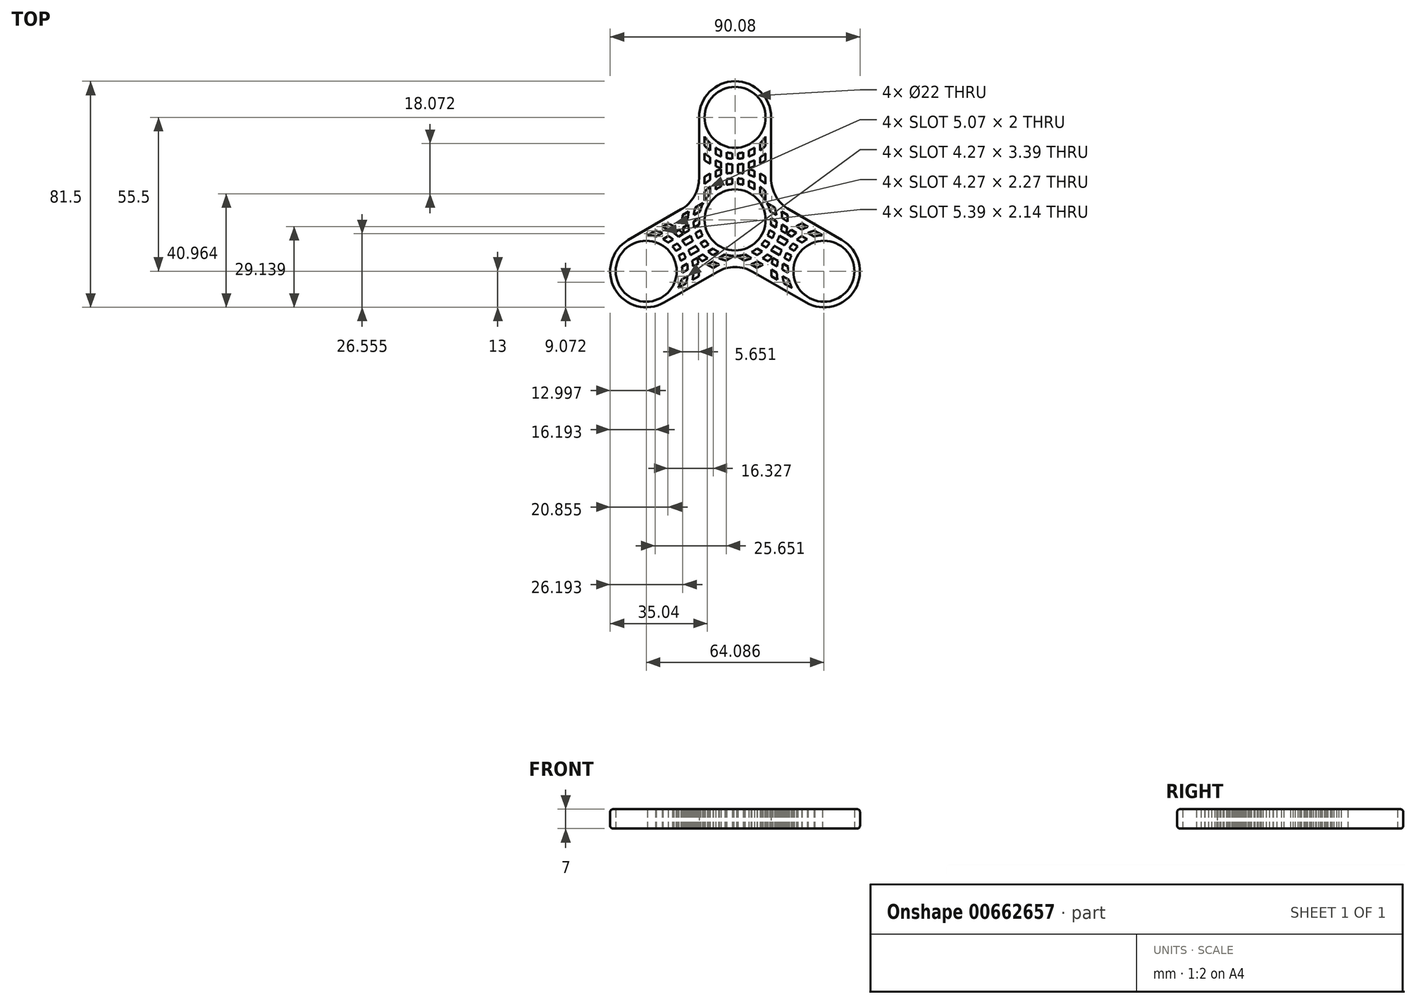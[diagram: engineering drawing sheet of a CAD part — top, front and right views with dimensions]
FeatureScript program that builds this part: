
annotation { "Feature Type Name" : "Feature", "Feature Type Description" : "" }
export const myFeature = defineFeature(function(context is Context, id is Id, definition is map)
    precondition{}
    {
        {
            var Q0;
            Q0=qCreatedBy(makeId("Top.planeOp"),FACE);
            var sketch = newSketch(context, id + "F0", { "sketchPlane" : qUnion([Q0])});
            skCircle(sketch, "E0", {"center": v(0, 0) * mm, "radius": 11 * mm});
            skCircle(sketch, "E1", {"center": v(0, 37) * mm, "radius": 11 * mm});
            skLineSegment(sketch, "E2", {"start": v(13, 37) * mm, "end": v(13, 15.01) * mm});
            skLineSegment(sketch, "E3.MirrorCS", {"start": v(-13, 37) * mm, "end": v(-13, 15.01) * mm});
            skLineSegment(sketch, "E4.1.0.0", {"start": v(-11, 30.07) * mm, "end": v(-11, 26.8) * mm});
            skLineSegment(sketch, "E4.2.0.0", {"start": v(-9, 27.62) * mm, "end": v(-9, 25) * mm});
            skLineSegment(sketch, "E4.3.0.0", {"start": v(-7, 26.05) * mm, "end": v(-7, 23.73) * mm});
            skLineSegment(sketch, "E4.4.0.0", {"start": v(-5, 25) * mm, "end": v(-5, 22.86) * mm});
            skLineSegment(sketch, "E4.5.0.0", {"start": v(-3, 24.35) * mm, "end": v(-3, 22.3) * mm});
            skLineSegment(sketch, "E4.6.0.0", {"start": v(-1, 24.04) * mm, "end": v(-1, 22.03) * mm});
            skLineSegment(sketch, "E4.7.0.0", {"start": v(1, 24.04) * mm, "end": v(1, 22.03) * mm});
            skLineSegment(sketch, "E4.8.0.0", {"start": v(3, 24.35) * mm, "end": v(3, 22.3) * mm});
            skLineSegment(sketch, "E4.9.0.0", {"start": v(5, 25) * mm, "end": v(5, 22.86) * mm});
            skLineSegment(sketch, "E4.10.0.0", {"start": v(7, 26.05) * mm, "end": v(7, 23.73) * mm});
            skLineSegment(sketch, "E4.11.0.0", {"start": v(9, 27.62) * mm, "end": v(9, 25) * mm});
            skLineSegment(sketch, "E4.12.0.0", {"start": v(11, 30.07) * mm, "end": v(11, 26.8) * mm});
            skArc(sketch, "E5", {"start": v(-11, 30.07) * mm, "mid": v(-10.07, 28.78) * mm, "end": v(-9, 27.62) * mm});
            skArc(sketch, "E6", {"start": v(-9, 9.38) * mm, "mid": v(-10.07, 8.22) * mm, "end": v(-11, 6.93) * mm});
            skArc(sketch, "E7.trimOffspring", {"start": v(13, 37) * mm, "mid": v(0, 50) * mm, "end": v(-13, 37) * mm});
            skArc(sketch, "E8.trimOffspring", {"start": v(9, 27.62) * mm, "mid": v(10.07, 28.78) * mm, "end": v(11, 30.07) * mm});
            skArc(sketch, "E9.trimOffspring", {"start": v(-7, 26.05) * mm, "mid": v(-6.02, 25.48) * mm, "end": v(-5, 25) * mm});
            skArc(sketch, "E10.trimOffspring", {"start": v(-3, 24.35) * mm, "mid": v(-2, 24.16) * mm, "end": v(-1, 24.04) * mm});
            skArc(sketch, "E11.trimOffspring", {"start": v(1, 24.04) * mm, "mid": v(2, 24.16) * mm, "end": v(3, 24.35) * mm});
            skArc(sketch, "E12.trimOffspring", {"start": v(5, 25) * mm, "mid": v(6.02, 25.48) * mm, "end": v(7, 26.05) * mm});
            skArc(sketch, "E13.trimOffspring", {"start": v(-5, 12) * mm, "mid": v(-6.02, 11.52) * mm, "end": v(-7, 10.95) * mm});
            skArc(sketch, "E14.trimOffspring", {"start": v(-1, 12.96) * mm, "mid": v(-2, 12.84) * mm, "end": v(-3, 12.65) * mm});
            skArc(sketch, "E15.trimOffspring", {"start": v(3, 12.65) * mm, "mid": v(2, 12.84) * mm, "end": v(1, 12.96) * mm});
            skArc(sketch, "E16.trimOffspring", {"start": v(7, 10.95) * mm, "mid": v(6.02, 11.52) * mm, "end": v(5, 12) * mm});
            skArc(sketch, "E17", {"start": v(11, 10.2) * mm, "mid": v(10.04, 11.14) * mm, "end": v(9, 12) * mm});
            skArc(sketch, "E18", {"start": v(-11, 26.8) * mm, "mid": v(-10.04, 25.86) * mm, "end": v(-9, 25) * mm});
            skArc(sketch, "E19", {"start": v(-11, 24.04) * mm, "mid": v(-10.03, 23.27) * mm, "end": v(-9, 22.58) * mm});
            skArc(sketch, "E20.trimOffspring", {"start": v(-7, 23.73) * mm, "mid": v(-6.02, 23.26) * mm, "end": v(-5, 22.86) * mm});
            skArc(sketch, "E21.trimOffspring", {"start": v(-7, 21.5) * mm, "mid": v(-6.01, 21.1) * mm, "end": v(-5, 20.75) * mm});
            skArc(sketch, "E22.trimOffspring", {"start": v(-3, 22.3) * mm, "mid": v(-2, 22.13) * mm, "end": v(-1, 22.03) * mm});
            skArc(sketch, "E23.trimOffspring", {"start": v(-3, 20.27) * mm, "mid": v(-2, 20.12) * mm, "end": v(-1, 20.03) * mm});
            skArc(sketch, "E24.trimOffspring", {"start": v(1, 20.03) * mm, "mid": v(2, 20.12) * mm, "end": v(3, 20.27) * mm});
            skArc(sketch, "E25.trimOffspring", {"start": v(1, 22.03) * mm, "mid": v(2, 22.13) * mm, "end": v(3, 22.3) * mm});
            skArc(sketch, "E26.trimOffspring", {"start": v(5, 22.86) * mm, "mid": v(6.02, 23.26) * mm, "end": v(7, 23.73) * mm});
            skArc(sketch, "E27.trimOffspring", {"start": v(5, 20.75) * mm, "mid": v(6.01, 21.1) * mm, "end": v(7, 21.5) * mm});
            skArc(sketch, "E28.trimOffspring", {"start": v(9, 25) * mm, "mid": v(10.04, 25.86) * mm, "end": v(11, 26.8) * mm});
            skArc(sketch, "E29.trimOffspring", {"start": v(9, 22.58) * mm, "mid": v(10.03, 23.27) * mm, "end": v(11, 24.04) * mm});
            skArc(sketch, "E30.trimOffspring", {"start": v(11, 12.96) * mm, "mid": v(10.03, 13.73) * mm, "end": v(9, 14.42) * mm});
            skArc(sketch, "E31.trimOffspring", {"start": v(-9, 14.42) * mm, "mid": v(-10.03, 13.73) * mm, "end": v(-11, 12.96) * mm});
            skArc(sketch, "E32.trimOffspring", {"start": v(-9, 12) * mm, "mid": v(-10.04, 11.14) * mm, "end": v(-11, 10.2) * mm});
            skArc(sketch, "E33.trimOffspring", {"start": v(-5, 14.14) * mm, "mid": v(-6.02, 13.74) * mm, "end": v(-7, 13.27) * mm});
            skArc(sketch, "E34.trimOffspring", {"start": v(-5, 16.25) * mm, "mid": v(-6.01, 15.9) * mm, "end": v(-7, 15.5) * mm});
            skArc(sketch, "E35.trimOffspring", {"start": v(-1, 16.97) * mm, "mid": v(-2, 16.88) * mm, "end": v(-3, 16.73) * mm});
            skArc(sketch, "E36.trimOffspring", {"start": v(-1, 14.97) * mm, "mid": v(-2, 14.87) * mm, "end": v(-3, 14.7) * mm});
            skArc(sketch, "E37.trimOffspring", {"start": v(3, 16.73) * mm, "mid": v(2, 16.88) * mm, "end": v(1, 16.97) * mm});
            skArc(sketch, "E38.trimOffspring", {"start": v(3, 14.7) * mm, "mid": v(2, 14.87) * mm, "end": v(1, 14.97) * mm});
            skArc(sketch, "E39.trimOffspring", {"start": v(7, 15.5) * mm, "mid": v(6.01, 15.9) * mm, "end": v(5, 16.25) * mm});
            skArc(sketch, "E40.trimOffspring", {"start": v(7, 13.27) * mm, "mid": v(6.02, 13.74) * mm, "end": v(5, 14.14) * mm});
            skLineSegment(sketch, "E41.trimOffspring", {"start": v(-11, 24.04) * mm, "end": v(-11, 21.5) * mm});
            skLineSegment(sketch, "E42.trimOffspring", {"start": v(-9, 22.58) * mm, "end": v(-9, 20.27) * mm});
            skLineSegment(sketch, "E43.trimOffspring", {"start": v(-7, 21.5) * mm, "end": v(-7, 19.34) * mm});
            skLineSegment(sketch, "E44.trimOffspring", {"start": v(-5, 20.75) * mm, "end": v(-5, 18.67) * mm});
            skLineSegment(sketch, "E45.trimOffspring", {"start": v(-3, 20.27) * mm, "end": v(-3, 16.73) * mm});
            skLineSegment(sketch, "E46.trimOffspring", {"start": v(-1, 20.03) * mm, "end": v(-1, 16.97) * mm});
            skLineSegment(sketch, "E47.trimOffspring", {"start": v(1, 20.03) * mm, "end": v(1, 16.97) * mm});
            skLineSegment(sketch, "E48.trimOffspring", {"start": v(3, 20.27) * mm, "end": v(3, 16.73) * mm});
            skLineSegment(sketch, "E49.trimOffspring", {"start": v(5, 20.75) * mm, "end": v(5, 18.67) * mm});
            skLineSegment(sketch, "E50.trimOffspring", {"start": v(7, 21.5) * mm, "end": v(7, 19.34) * mm});
            skLineSegment(sketch, "E51.trimOffspring", {"start": v(9, 22.58) * mm, "end": v(9, 20.27) * mm});
            skLineSegment(sketch, "E52.trimOffspring", {"start": v(11, 24.04) * mm, "end": v(11, 21.5) * mm});
            skLineSegment(sketch, "E53.trimOffspring", {"start": v(-11, 10.2) * mm, "end": v(-11, 6.93) * mm});
            skLineSegment(sketch, "E54.trimOffspring", {"start": v(-7, 13.27) * mm, "end": v(-7, 10.95) * mm});
            skLineSegment(sketch, "E55.trimOffspring", {"start": v(-3, 14.7) * mm, "end": v(-3, 12.65) * mm});
            skLineSegment(sketch, "E56.trimOffspring", {"start": v(1, 14.97) * mm, "end": v(1, 12.96) * mm});
            skLineSegment(sketch, "E57.trimOffspring", {"start": v(5, 14.14) * mm, "end": v(5, 12) * mm});
            skLineSegment(sketch, "E58.trimOffspring", {"start": v(9, 12) * mm, "end": v(9, 9.38) * mm});
            skLineSegment(sketch, "E59.trimOffspring", {"start": v(-9, 12) * mm, "end": v(-9, 9.38) * mm});
            skLineSegment(sketch, "E60.trimOffspring", {"start": v(-5, 14.14) * mm, "end": v(-5, 12) * mm});
            skLineSegment(sketch, "E61.trimOffspring", {"start": v(-1, 14.97) * mm, "end": v(-1, 12.96) * mm});
            skLineSegment(sketch, "E62.trimOffspring", {"start": v(3, 14.7) * mm, "end": v(3, 12.65) * mm});
            skLineSegment(sketch, "E63.trimOffspring", {"start": v(7, 13.27) * mm, "end": v(7, 10.95) * mm});
            skLineSegment(sketch, "E64.trimOffspring", {"start": v(11, 10.2) * mm, "end": v(11, 6.93) * mm});
            skArc(sketch, "E65", {"start": v(-11, 21.5) * mm, "mid": v(-10.02, 20.86) * mm, "end": v(-9, 20.27) * mm});
            skArc(sketch, "E66.trimOffspring", {"start": v(11, 15.5) * mm, "mid": v(10.02, 16.14) * mm, "end": v(9, 16.73) * mm});
            skArc(sketch, "E67.trimOffspring", {"start": v(-7, 19.34) * mm, "mid": v(-6, 18.98) * mm, "end": v(-5, 18.67) * mm});
            skArc(sketch, "E68.trimOffspring", {"start": v(-9, 16.73) * mm, "mid": v(-10.02, 16.14) * mm, "end": v(-11, 15.5) * mm});
            skArc(sketch, "E69.trimOffspring", {"start": v(9, 20.27) * mm, "mid": v(10.02, 20.86) * mm, "end": v(11, 21.5) * mm});
            skArc(sketch, "E70.trimOffspring", {"start": v(7, 17.66) * mm, "mid": v(6, 18.02) * mm, "end": v(5, 18.33) * mm});
            skArc(sketch, "E71.trimOffspring", {"start": v(-5, 18.33) * mm, "mid": v(-6, 18.02) * mm, "end": v(-7, 17.66) * mm});
            skArc(sketch, "E72.trimOffspring", {"start": v(5, 18.67) * mm, "mid": v(6, 18.98) * mm, "end": v(7, 19.34) * mm});
            skLineSegment(sketch, "E73.trimOffspring", {"start": v(-11, 15.5) * mm, "end": v(-11, 12.96) * mm});
            skLineSegment(sketch, "E74.trimOffspring", {"start": v(-9, 16.73) * mm, "end": v(-9, 14.42) * mm});
            skLineSegment(sketch, "E75.trimOffspring", {"start": v(11, 15.5) * mm, "end": v(11, 12.96) * mm});
            skLineSegment(sketch, "E76.trimOffspring", {"start": v(9, 16.73) * mm, "end": v(9, 14.42) * mm});
            skLineSegment(sketch, "E77.trimOffspring", {"start": v(-7, 17.66) * mm, "end": v(-7, 15.5) * mm});
            skLineSegment(sketch, "E78.trimOffspring", {"start": v(-5, 18.33) * mm, "end": v(-5, 16.25) * mm});
            skLineSegment(sketch, "E79.trimOffspring", {"start": v(5, 18.33) * mm, "end": v(5, 16.25) * mm});
            skLineSegment(sketch, "E80.trimOffspring", {"start": v(7, 17.66) * mm, "end": v(7, 15.5) * mm});
            skArc(sketch, "E81.trimOffspring", {"start": v(11, 6.93) * mm, "mid": v(10.07, 8.22) * mm, "end": v(9, 9.38) * mm});
            skCircle(sketch, "E82.1.0", {"center": v(-32.04, -18.5) * mm, "radius": 11 * mm});
            skLineSegment(sketch, "E82.1.1", {"start": v(-31.54, -5.5) * mm, "end": v(-28.71, -3.87) * mm});
            skLineSegment(sketch, "E82.1.2", {"start": v(-38.54, -7.24) * mm, "end": v(-19.5, 3.75) * mm});
            skLineSegment(sketch, "E82.1.3", {"start": v(-25.54, -29.76) * mm, "end": v(-6.5, -18.76) * mm});
            skLineSegment(sketch, "E82.1.4", {"start": v(-20.54, -24.56) * mm, "end": v(-17.71, -22.93) * mm});
            skArc(sketch, "E82.1.5", {"start": v(-38.54, -7.24) * mm, "mid": v(-43.3, -25) * mm, "end": v(-25.54, -29.76) * mm});
            skLineSegment(sketch, "E82.1.6", {"start": v(-14.33, 4.43) * mm, "end": v(-11.5, 6.06) * mm});
            skLineSegment(sketch, "E82.1.7", {"start": v(-19.05, -7.54) * mm, "end": v(-16, -5.77) * mm});
            skArc(sketch, "E82.1.8", {"start": v(-20.54, -24.56) * mm, "mid": v(-19.9, -23.12) * mm, "end": v(-19.42, -21.6) * mm});
            skLineSegment(sketch, "E82.1.9", {"start": v(-3.33, -14.63) * mm, "end": v(-0.5, -13) * mm});
            skLineSegment(sketch, "E82.1.10", {"start": v(-16.05, -12.73) * mm, "end": v(-13, -10.96) * mm});
            skArc(sketch, "E82.1.11", {"start": v(-28.42, -6.02) * mm, "mid": v(-29.97, -5.67) * mm, "end": v(-31.54, -5.5) * mm});
            skLineSegment(sketch, "E82.1.12", {"start": v(-17.85, -9.15) * mm, "end": v(-15.2, -7.62) * mm});
            skLineSegment(sketch, "E82.1.13", {"start": v(-16.85, -10.88) * mm, "end": v(-14.2, -9.35) * mm});
            skLineSegment(sketch, "E82.1.14", {"start": v(-10, -16.16) * mm, "end": v(-7.99, -15) * mm});
            skLineSegment(sketch, "E82.1.15", {"start": v(-11.23, -9.95) * mm, "end": v(-9.45, -8.92) * mm});
            skArc(sketch, "E82.1.16", {"start": v(-14.33, 4.43) * mm, "mid": v(-14.67, 3.12) * mm, "end": v(-14.9, 1.8) * mm});
            skLineSegment(sketch, "E82.1.17", {"start": v(-22.13, -4.7) * mm, "end": v(-20.25, -3.6) * mm});
            skArc(sketch, "E82.1.18", {"start": v(-20.47, -6.05) * mm, "mid": v(-21.28, -5.34) * mm, "end": v(-22.13, -4.7) * mm});
            skArc(sketch, "E82.1.19", {"start": v(-24.15, -8.17) * mm, "mid": v(-25.08, -7.52) * mm, "end": v(-26.06, -6.96) * mm});
            skLineSegment(sketch, "E82.1.20", {"start": v(-15.13, -16.82) * mm, "end": v(-13.25, -15.73) * mm});
            skLineSegment(sketch, "E82.1.21", {"start": v(-26.32, -2.5) * mm, "end": v(-24.13, -1.23) * mm});
            skArc(sketch, "E82.1.22", {"start": v(-12.46, -8.35) * mm, "mid": v(-11.87, -9.17) * mm, "end": v(-11.23, -9.95) * mm});
            skLineSegment(sketch, "E82.1.23", {"start": v(-22.59, -9.58) * mm, "end": v(-20.82, -8.55) * mm});
            skLineSegment(sketch, "E82.1.24", {"start": v(-26.06, -6.96) * mm, "end": v(-24.05, -5.8) * mm});
            skArc(sketch, "E82.1.25", {"start": v(-10, -16.16) * mm, "mid": v(-8.97, -16.75) * mm, "end": v(-7.92, -17.27) * mm});
            skLineSegment(sketch, "E82.1.26", {"start": v(-18.92, 1.78) * mm, "end": v(-16.72, 3.05) * mm});
            skArc(sketch, "E82.1.27", {"start": v(-19.59, -14.77) * mm, "mid": v(-19.92, -13.82) * mm, "end": v(-20.32, -12.89) * mm});
            skLineSegment(sketch, "E82.1.28", {"start": v(-5.9, -13.8) * mm, "end": v(-3.62, -12.48) * mm});
            skArc(sketch, "E82.1.29", {"start": v(-21.32, -11.15) * mm, "mid": v(-21.92, -10.34) * mm, "end": v(-22.59, -9.58) * mm});
            skLineSegment(sketch, "E82.1.30", {"start": v(-15.47, -14.7) * mm, "end": v(-13.67, -13.66) * mm});
            skArc(sketch, "E82.1.31", {"start": v(-19.58, -10.15) * mm, "mid": v(-20.17, -9.33) * mm, "end": v(-20.82, -8.55) * mm});
            skArc(sketch, "E82.1.32", {"start": v(-16.92, -1.68) * mm, "mid": v(-16.78, -2.74) * mm, "end": v(-16.57, -3.8) * mm});
            skLineSegment(sketch, "E82.1.33", {"start": v(-20.47, -6.05) * mm, "end": v(-18.67, -5) * mm});
            skArc(sketch, "E82.1.34", {"start": v(-9.75, -11.4) * mm, "mid": v(-8.9, -12.08) * mm, "end": v(-7.99, -12.7) * mm});
            skArc(sketch, "E82.1.35", {"start": v(-13.37, -13.5) * mm, "mid": v(-12.6, -14.22) * mm, "end": v(-11.8, -14.9) * mm});
            skArc(sketch, "E82.1.36", {"start": v(-11.5, 6.06) * mm, "mid": v(-12.15, 4.62) * mm, "end": v(-12.62, 3.1) * mm});
            skArc(sketch, "E82.1.37", {"start": v(-13.13, -20.28) * mm, "mid": v(-13.05, -19.1) * mm, "end": v(-13.05, -17.93) * mm});
            skArc(sketch, "E82.1.38", {"start": v(-13.25, -15.73) * mm, "mid": v(-13.43, -14.7) * mm, "end": v(-13.67, -13.66) * mm});
            skLineSegment(sketch, "E82.1.39", {"start": v(-14.9, 1.8) * mm, "end": v(-12.62, 3.1) * mm});
            skArc(sketch, "E82.1.40", {"start": v(-17.71, -22.93) * mm, "mid": v(-17.37, -21.62) * mm, "end": v(-17.15, -20.3) * mm});
            skArc(sketch, "E82.1.41", {"start": v(-14.2, -9.35) * mm, "mid": v(-13.62, -10.18) * mm, "end": v(-13, -10.96) * mm});
            skLineSegment(sketch, "E82.1.42", {"start": v(-24.05, -3.5) * mm, "end": v(-22.05, -2.34) * mm});
            skArc(sketch, "E82.1.43", {"start": v(-22.3, -7.1) * mm, "mid": v(-23.15, -6.42) * mm, "end": v(-24.05, -5.8) * mm});
            skArc(sketch, "E82.1.44", {"start": v(-17.05, -17.93) * mm, "mid": v(-17.14, -16.84) * mm, "end": v(-17.3, -15.76) * mm});
            skLineSegment(sketch, "E82.1.45", {"start": v(-15.05, -19.08) * mm, "end": v(-13.05, -17.93) * mm});
            skLineSegment(sketch, "E82.1.46", {"start": v(-28.42, -6.02) * mm, "end": v(-26.15, -4.7) * mm});
            skArc(sketch, "E82.1.47", {"start": v(-15.32, -21.55) * mm, "mid": v(-15.14, -20.32) * mm, "end": v(-15.05, -19.08) * mm});
            skLineSegment(sketch, "E82.1.48", {"start": v(-19.42, -21.6) * mm, "end": v(-17.15, -20.3) * mm});
            skArc(sketch, "E82.1.49", {"start": v(-5.9, -13.8) * mm, "mid": v(-4.63, -14.27) * mm, "end": v(-3.33, -14.63) * mm});
            skLineSegment(sketch, "E82.1.50", {"start": v(-21.32, -11.15) * mm, "end": v(-19.58, -10.15) * mm});
            skLineSegment(sketch, "E82.1.51", {"start": v(-19.06, -19.08) * mm, "end": v(-17.05, -17.93) * mm});
            skLineSegment(sketch, "E82.1.52", {"start": v(-19.15, -16.83) * mm, "end": v(-17.3, -15.76) * mm});
            skLineSegment(sketch, "E82.1.53", {"start": v(-19.59, -14.77) * mm, "end": v(-17.82, -13.75) * mm});
            skLineSegment(sketch, "E82.1.54", {"start": v(-20.32, -12.89) * mm, "end": v(-18.58, -11.88) * mm});
            skArc(sketch, "E82.1.55", {"start": v(-16.05, -12.73) * mm, "mid": v(-16.42, -11.8) * mm, "end": v(-16.85, -10.88) * mm});
            skLineSegment(sketch, "E82.1.56", {"start": v(-15.32, -21.55) * mm, "end": v(-13.13, -20.28) * mm});
            skLineSegment(sketch, "E82.1.57", {"start": v(-24.15, -8.17) * mm, "end": v(-22.3, -7.1) * mm});
            skArc(sketch, "E82.1.58", {"start": v(-11.57, -12.45) * mm, "mid": v(-10.77, -13.16) * mm, "end": v(-9.92, -13.8) * mm});
            skLineSegment(sketch, "E82.1.59", {"start": v(-14.75, -2.74) * mm, "end": v(-12.9, -1.67) * mm});
            skArc(sketch, "E82.1.60", {"start": v(-18.92, 1.78) * mm, "mid": v(-19, 0.6) * mm, "end": v(-19, -0.57) * mm});
            skArc(sketch, "E82.1.61", {"start": v(-19.06, -19.08) * mm, "mid": v(-19.05, -17.96) * mm, "end": v(-19.15, -16.83) * mm});
            skLineSegment(sketch, "E82.1.62", {"start": v(-7.92, -17.27) * mm, "end": v(-5.72, -16) * mm});
            skArc(sketch, "E82.1.63", {"start": v(-26.15, -4.7) * mm, "mid": v(-27.41, -4.23) * mm, "end": v(-28.71, -3.87) * mm});
            skLineSegment(sketch, "E82.1.64", {"start": v(-18.8, -2.77) * mm, "end": v(-16.92, -1.68) * mm});
            skLineSegment(sketch, "E82.1.65", {"start": v(-19, -0.57) * mm, "end": v(-16.99, 0.58) * mm});
            skLineSegment(sketch, "E82.1.66", {"start": v(-9.75, -11.4) * mm, "end": v(-7.9, -10.33) * mm});
            skArc(sketch, "E82.1.67", {"start": v(-12.99, 0.58) * mm, "mid": v(-12.99, -0.54) * mm, "end": v(-12.9, -1.67) * mm});
            skArc(sketch, "E82.1.68", {"start": v(-22.05, -2.34) * mm, "mid": v(-23.07, -1.75) * mm, "end": v(-24.13, -1.23) * mm});
            skArc(sketch, "E82.1.69", {"start": v(-16, -5.77) * mm, "mid": v(-15.62, -6.7) * mm, "end": v(-15.2, -7.62) * mm});
            skArc(sketch, "E82.1.70", {"start": v(-15.13, -16.82) * mm, "mid": v(-15.27, -15.76) * mm, "end": v(-15.47, -14.7) * mm});
            skArc(sketch, "E82.1.71", {"start": v(-24.05, -3.5) * mm, "mid": v(-25.17, -2.95) * mm, "end": v(-26.32, -2.5) * mm});
            skArc(sketch, "E82.1.72", {"start": v(-17.85, -9.15) * mm, "mid": v(-18.42, -8.32) * mm, "end": v(-19.05, -7.54) * mm});
            skArc(sketch, "E82.1.73", {"start": v(-7.9, -10.33) * mm, "mid": v(-6.97, -10.98) * mm, "end": v(-5.99, -11.54) * mm});
            skLineSegment(sketch, "E82.1.74", {"start": v(-11.8, -14.9) * mm, "end": v(-9.92, -13.8) * mm});
            skLineSegment(sketch, "E82.1.75", {"start": v(-12.46, -8.35) * mm, "end": v(-10.72, -7.35) * mm});
            skArc(sketch, "E82.1.76", {"start": v(-14.99, -0.57) * mm, "mid": v(-14.9, -1.66) * mm, "end": v(-14.75, -2.74) * mm});
            skLineSegment(sketch, "E82.1.77", {"start": v(-13.46, -6.62) * mm, "end": v(-11.72, -5.61) * mm});
            skLineSegment(sketch, "E82.1.78", {"start": v(-14.23, -4.75) * mm, "end": v(-12.45, -3.73) * mm});
            skArc(sketch, "E82.1.79", {"start": v(-18.67, -5) * mm, "mid": v(-19.44, -4.28) * mm, "end": v(-20.25, -3.6) * mm});
            skArc(sketch, "E82.1.80", {"start": v(-18.8, -2.77) * mm, "mid": v(-18.61, -3.8) * mm, "end": v(-18.37, -4.84) * mm});
            skLineSegment(sketch, "E82.1.81", {"start": v(-14.99, -0.57) * mm, "end": v(-12.99, 0.58) * mm});
            skLineSegment(sketch, "E82.1.82", {"start": v(-13.37, -13.5) * mm, "end": v(-11.57, -12.45) * mm});
            skLineSegment(sketch, "E82.1.83", {"start": v(-18.37, -4.84) * mm, "end": v(-16.57, -3.8) * mm});
            skArc(sketch, "E82.1.84", {"start": v(-12.45, -3.73) * mm, "mid": v(-12.13, -4.68) * mm, "end": v(-11.72, -5.61) * mm});
            skArc(sketch, "E82.1.85", {"start": v(-7.99, -15) * mm, "mid": v(-6.88, -15.55) * mm, "end": v(-5.72, -16) * mm});
            skArc(sketch, "E82.1.86", {"start": v(-3.62, -12.48) * mm, "mid": v(-2.08, -12.83) * mm, "end": v(-0.5, -13) * mm});
            skLineSegment(sketch, "E82.1.87", {"start": v(-7.99, -12.7) * mm, "end": v(-5.99, -11.54) * mm});
            skArc(sketch, "E82.1.88", {"start": v(-17.82, -13.75) * mm, "mid": v(-18.17, -12.8) * mm, "end": v(-18.58, -11.88) * mm});
            skArc(sketch, "E82.1.89", {"start": v(-14.23, -4.75) * mm, "mid": v(-13.88, -5.7) * mm, "end": v(-13.46, -6.62) * mm});
            skArc(sketch, "E82.1.90", {"start": v(-16.72, 3.05) * mm, "mid": v(-16.9, 1.82) * mm, "end": v(-16.99, 0.58) * mm});
            skArc(sketch, "E82.1.91", {"start": v(-10.72, -7.35) * mm, "mid": v(-10.12, -8.16) * mm, "end": v(-9.45, -8.92) * mm});
            skCircle(sketch, "E82.2.0", {"center": v(32.04, -18.5) * mm, "radius": 11 * mm});
            skLineSegment(sketch, "E82.2.1", {"start": v(20.54, -24.56) * mm, "end": v(17.71, -22.93) * mm});
            skLineSegment(sketch, "E82.2.2", {"start": v(25.54, -29.76) * mm, "end": v(6.5, -18.76) * mm});
            skLineSegment(sketch, "E82.2.3", {"start": v(38.54, -7.24) * mm, "end": v(19.5, 3.75) * mm});
            skLineSegment(sketch, "E82.2.4", {"start": v(31.54, -5.5) * mm, "end": v(28.71, -3.87) * mm});
            skArc(sketch, "E82.2.5", {"start": v(25.54, -29.76) * mm, "mid": v(43.3, -25) * mm, "end": v(38.54, -7.24) * mm});
            skLineSegment(sketch, "E82.2.6", {"start": v(3.33, -14.63) * mm, "end": v(0.5, -13) * mm});
            skLineSegment(sketch, "E82.2.7", {"start": v(16.05, -12.73) * mm, "end": v(13, -10.96) * mm});
            skArc(sketch, "E82.2.8", {"start": v(31.54, -5.5) * mm, "mid": v(29.97, -5.67) * mm, "end": v(28.42, -6.02) * mm});
            skLineSegment(sketch, "E82.2.9", {"start": v(14.33, 4.43) * mm, "end": v(11.5, 6.06) * mm});
            skLineSegment(sketch, "E82.2.10", {"start": v(19.05, -7.54) * mm, "end": v(16, -5.77) * mm});
            skArc(sketch, "E82.2.11", {"start": v(19.42, -21.6) * mm, "mid": v(19.9, -23.12) * mm, "end": v(20.54, -24.56) * mm});
            skLineSegment(sketch, "E82.2.12", {"start": v(16.85, -10.88) * mm, "end": v(14.2, -9.35) * mm});
            skLineSegment(sketch, "E82.2.13", {"start": v(17.85, -9.15) * mm, "end": v(15.2, -7.62) * mm});
            skLineSegment(sketch, "E82.2.14", {"start": v(19, -0.57) * mm, "end": v(16.99, 0.58) * mm});
            skLineSegment(sketch, "E82.2.15", {"start": v(14.23, -4.75) * mm, "end": v(12.45, -3.73) * mm});
            skArc(sketch, "E82.2.16", {"start": v(3.33, -14.63) * mm, "mid": v(4.63, -14.27) * mm, "end": v(5.9, -13.8) * mm});
            skLineSegment(sketch, "E82.2.17", {"start": v(15.13, -16.82) * mm, "end": v(13.25, -15.73) * mm});
            skArc(sketch, "E82.2.18", {"start": v(15.47, -14.7) * mm, "mid": v(15.27, -15.76) * mm, "end": v(15.13, -16.82) * mm});
            skArc(sketch, "E82.2.19", {"start": v(19.15, -16.83) * mm, "mid": v(19.05, -17.96) * mm, "end": v(19.06, -19.08) * mm});
            skLineSegment(sketch, "E82.2.20", {"start": v(22.13, -4.7) * mm, "end": v(20.25, -3.6) * mm});
            skLineSegment(sketch, "E82.2.21", {"start": v(15.32, -21.55) * mm, "end": v(13.13, -20.28) * mm});
            skArc(sketch, "E82.2.22", {"start": v(13.46, -6.62) * mm, "mid": v(13.88, -5.7) * mm, "end": v(14.23, -4.75) * mm});
            skLineSegment(sketch, "E82.2.23", {"start": v(19.59, -14.77) * mm, "end": v(17.82, -13.75) * mm});
            skLineSegment(sketch, "E82.2.24", {"start": v(19.06, -19.08) * mm, "end": v(17.05, -17.93) * mm});
            skArc(sketch, "E82.2.25", {"start": v(19, -0.57) * mm, "mid": v(19, 0.6) * mm, "end": v(18.92, 1.78) * mm});
            skLineSegment(sketch, "E82.2.26", {"start": v(7.92, -17.27) * mm, "end": v(5.72, -16) * mm});
            skArc(sketch, "E82.2.27", {"start": v(22.59, -9.58) * mm, "mid": v(21.92, -10.34) * mm, "end": v(21.32, -11.15) * mm});
            skLineSegment(sketch, "E82.2.28", {"start": v(14.9, 1.8) * mm, "end": v(12.62, 3.1) * mm});
            skArc(sketch, "E82.2.29", {"start": v(20.32, -12.89) * mm, "mid": v(19.92, -13.82) * mm, "end": v(19.59, -14.77) * mm});
            skLineSegment(sketch, "E82.2.30", {"start": v(20.47, -6.05) * mm, "end": v(18.67, -5) * mm});
            skArc(sketch, "E82.2.31", {"start": v(18.58, -11.88) * mm, "mid": v(18.17, -12.8) * mm, "end": v(17.82, -13.75) * mm});
            skArc(sketch, "E82.2.32", {"start": v(9.92, -13.8) * mm, "mid": v(10.77, -13.16) * mm, "end": v(11.57, -12.45) * mm});
            skLineSegment(sketch, "E82.2.33", {"start": v(15.47, -14.7) * mm, "end": v(13.67, -13.66) * mm});
            skArc(sketch, "E82.2.34", {"start": v(14.75, -2.74) * mm, "mid": v(14.9, -1.66) * mm, "end": v(14.99, -0.57) * mm});
            skArc(sketch, "E82.2.35", {"start": v(18.37, -4.84) * mm, "mid": v(18.61, -3.8) * mm, "end": v(18.8, -2.77) * mm});
            skArc(sketch, "E82.2.36", {"start": v(0.5, -13) * mm, "mid": v(2.08, -12.83) * mm, "end": v(3.62, -12.48) * mm});
            skArc(sketch, "E82.2.37", {"start": v(24.13, -1.23) * mm, "mid": v(23.07, -1.75) * mm, "end": v(22.05, -2.34) * mm});
            skArc(sketch, "E82.2.38", {"start": v(20.25, -3.6) * mm, "mid": v(19.44, -4.28) * mm, "end": v(18.67, -5) * mm});
            skLineSegment(sketch, "E82.2.39", {"start": v(5.9, -13.8) * mm, "end": v(3.62, -12.48) * mm});
            skArc(sketch, "E82.2.40", {"start": v(28.71, -3.87) * mm, "mid": v(27.41, -4.23) * mm, "end": v(26.15, -4.7) * mm});
            skArc(sketch, "E82.2.41", {"start": v(15.2, -7.62) * mm, "mid": v(15.62, -6.7) * mm, "end": v(16, -5.77) * mm});
            skLineSegment(sketch, "E82.2.42", {"start": v(15.05, -19.08) * mm, "end": v(13.05, -17.93) * mm});
            skArc(sketch, "E82.2.43", {"start": v(17.3, -15.76) * mm, "mid": v(17.14, -16.84) * mm, "end": v(17.05, -17.93) * mm});
            skArc(sketch, "E82.2.44", {"start": v(24.05, -5.8) * mm, "mid": v(23.15, -6.42) * mm, "end": v(22.3, -7.1) * mm});
            skLineSegment(sketch, "E82.2.45", {"start": v(24.05, -3.5) * mm, "end": v(22.05, -2.34) * mm});
            skLineSegment(sketch, "E82.2.46", {"start": v(19.42, -21.6) * mm, "end": v(17.15, -20.3) * mm});
            skArc(sketch, "E82.2.47", {"start": v(26.32, -2.5) * mm, "mid": v(25.17, -2.95) * mm, "end": v(24.05, -3.5) * mm});
            skLineSegment(sketch, "E82.2.48", {"start": v(28.42, -6.02) * mm, "end": v(26.15, -4.7) * mm});
            skArc(sketch, "E82.2.49", {"start": v(14.9, 1.8) * mm, "mid": v(14.67, 3.12) * mm, "end": v(14.33, 4.43) * mm});
            skLineSegment(sketch, "E82.2.50", {"start": v(20.32, -12.89) * mm, "end": v(18.58, -11.88) * mm});
            skLineSegment(sketch, "E82.2.51", {"start": v(26.06, -6.96) * mm, "end": v(24.05, -5.8) * mm});
            skLineSegment(sketch, "E82.2.52", {"start": v(24.15, -8.17) * mm, "end": v(22.3, -7.1) * mm});
            skLineSegment(sketch, "E82.2.53", {"start": v(22.59, -9.58) * mm, "end": v(20.82, -8.55) * mm});
            skLineSegment(sketch, "E82.2.54", {"start": v(21.32, -11.15) * mm, "end": v(19.58, -10.15) * mm});
            skArc(sketch, "E82.2.55", {"start": v(19.05, -7.54) * mm, "mid": v(18.42, -8.32) * mm, "end": v(17.85, -9.15) * mm});
            skLineSegment(sketch, "E82.2.56", {"start": v(26.32, -2.5) * mm, "end": v(24.13, -1.23) * mm});
            skLineSegment(sketch, "E82.2.57", {"start": v(19.15, -16.83) * mm, "end": v(17.3, -15.76) * mm});
            skArc(sketch, "E82.2.58", {"start": v(16.57, -3.8) * mm, "mid": v(16.78, -2.74) * mm, "end": v(16.92, -1.68) * mm});
            skLineSegment(sketch, "E82.2.59", {"start": v(9.75, -11.4) * mm, "end": v(7.9, -10.33) * mm});
            skArc(sketch, "E82.2.60", {"start": v(7.92, -17.27) * mm, "mid": v(8.97, -16.75) * mm, "end": v(10, -16.16) * mm});
            skArc(sketch, "E82.2.61", {"start": v(26.06, -6.96) * mm, "mid": v(25.08, -7.52) * mm, "end": v(24.15, -8.17) * mm});
            skLineSegment(sketch, "E82.2.62", {"start": v(18.92, 1.78) * mm, "end": v(16.72, 3.05) * mm});
            skArc(sketch, "E82.2.63", {"start": v(17.15, -20.3) * mm, "mid": v(17.37, -21.62) * mm, "end": v(17.71, -22.93) * mm});
            skLineSegment(sketch, "E82.2.64", {"start": v(11.8, -14.9) * mm, "end": v(9.92, -13.8) * mm});
            skLineSegment(sketch, "E82.2.65", {"start": v(10, -16.16) * mm, "end": v(7.99, -15) * mm});
            skLineSegment(sketch, "E82.2.66", {"start": v(14.75, -2.74) * mm, "end": v(12.9, -1.67) * mm});
            skArc(sketch, "E82.2.67", {"start": v(5.99, -11.54) * mm, "mid": v(6.97, -10.98) * mm, "end": v(7.9, -10.33) * mm});
            skArc(sketch, "E82.2.68", {"start": v(13.05, -17.93) * mm, "mid": v(13.05, -19.1) * mm, "end": v(13.13, -20.28) * mm});
            skArc(sketch, "E82.2.69", {"start": v(13, -10.96) * mm, "mid": v(13.62, -10.18) * mm, "end": v(14.2, -9.35) * mm});
            skArc(sketch, "E82.2.70", {"start": v(22.13, -4.7) * mm, "mid": v(21.28, -5.34) * mm, "end": v(20.47, -6.05) * mm});
            skArc(sketch, "E82.2.71", {"start": v(15.05, -19.08) * mm, "mid": v(15.14, -20.32) * mm, "end": v(15.32, -21.55) * mm});
            skArc(sketch, "E82.2.72", {"start": v(16.85, -10.88) * mm, "mid": v(16.42, -11.8) * mm, "end": v(16.05, -12.73) * mm});
            skArc(sketch, "E82.2.73", {"start": v(12.9, -1.67) * mm, "mid": v(12.99, -0.54) * mm, "end": v(12.99, 0.58) * mm});
            skLineSegment(sketch, "E82.2.74", {"start": v(18.8, -2.77) * mm, "end": v(16.92, -1.68) * mm});
            skLineSegment(sketch, "E82.2.75", {"start": v(13.46, -6.62) * mm, "end": v(11.72, -5.61) * mm});
            skArc(sketch, "E82.2.76", {"start": v(7.99, -12.7) * mm, "mid": v(8.9, -12.08) * mm, "end": v(9.75, -11.4) * mm});
            skLineSegment(sketch, "E82.2.77", {"start": v(12.46, -8.35) * mm, "end": v(10.72, -7.35) * mm});
            skLineSegment(sketch, "E82.2.78", {"start": v(11.23, -9.95) * mm, "end": v(9.45, -8.92) * mm});
            skArc(sketch, "E82.2.79", {"start": v(13.67, -13.66) * mm, "mid": v(13.43, -14.7) * mm, "end": v(13.25, -15.73) * mm});
            skArc(sketch, "E82.2.80", {"start": v(11.8, -14.9) * mm, "mid": v(12.6, -14.22) * mm, "end": v(13.37, -13.5) * mm});
            skLineSegment(sketch, "E82.2.81", {"start": v(7.99, -12.7) * mm, "end": v(5.99, -11.54) * mm});
            skLineSegment(sketch, "E82.2.82", {"start": v(18.37, -4.84) * mm, "end": v(16.57, -3.8) * mm});
            skLineSegment(sketch, "E82.2.83", {"start": v(13.37, -13.5) * mm, "end": v(11.57, -12.45) * mm});
            skArc(sketch, "E82.2.84", {"start": v(9.45, -8.92) * mm, "mid": v(10.12, -8.16) * mm, "end": v(10.72, -7.35) * mm});
            skArc(sketch, "E82.2.85", {"start": v(16.99, 0.58) * mm, "mid": v(16.9, 1.82) * mm, "end": v(16.72, 3.05) * mm});
            skArc(sketch, "E82.2.86", {"start": v(12.62, 3.1) * mm, "mid": v(12.15, 4.62) * mm, "end": v(11.5, 6.06) * mm});
            skLineSegment(sketch, "E82.2.87", {"start": v(14.99, -0.57) * mm, "end": v(12.99, 0.58) * mm});
            skArc(sketch, "E82.2.88", {"start": v(20.82, -8.55) * mm, "mid": v(20.17, -9.33) * mm, "end": v(19.58, -10.15) * mm});
            skArc(sketch, "E82.2.89", {"start": v(11.23, -9.95) * mm, "mid": v(11.87, -9.17) * mm, "end": v(12.46, -8.35) * mm});
            skArc(sketch, "E82.2.90", {"start": v(5.72, -16) * mm, "mid": v(6.88, -15.55) * mm, "end": v(7.99, -15) * mm});
            skArc(sketch, "E82.2.91", {"start": v(11.72, -5.61) * mm, "mid": v(12.13, -4.68) * mm, "end": v(12.45, -3.73) * mm});
            skPoint(sketch, "E83.visualSharp", {"position": v(13, 7.5) * mm});
            skArc(sketch, "E83.filletArc", {"start": v(13, 15.01) * mm, "mid": v(14.74, 8.51) * mm, "end": v(19.5, 3.75) * mm});
            skPoint(sketch, "E84.visualSharp", {"position": v(0, -15.01) * mm});
            skArc(sketch, "E84.filletArc", {"start": v(6.5, -18.76) * mm, "mid": v(0, -17.02) * mm, "end": v(-6.5, -18.76) * mm});
            skPoint(sketch, "E85.visualSharp", {"position": v(-13, 7.5) * mm});
            skArc(sketch, "E85.filletArc", {"start": v(-19.5, 3.75) * mm, "mid": v(-14.74, 8.51) * mm, "end": v(-13, 15.01) * mm});
            skSolve(sketch);
        }
        {
            var Q0;
            Q0 = qSketchRegion(id + "F0", true);
            extrude(context, id + "F1", {"entities" : qUnion([Q0]), "depth" : 7 * mm, "offsetDistance" : 25 * mm});
        }
        {
            var Q0;
            Q0=makeQuery(id+"F1.opExtrude","CAP_EDGE",EDGE,{"disambiguationData":[OSD([sQuery(id+"F0.wireOp",EDGE,"E7.trimOffspring")])],"isStart":false});
            fillet(context, id + "F2", {"entities" : qUnion([Q0]), "radius" : 1 * mm, "tangentPropagation" : true, "allowEdgeOverflow" : false});
        }
        {
            var Q0;
            Q0=makeQuery(id+"F1.opExtrude","CAP_EDGE",EDGE,{"disambiguationData":[OSD([sQuery(id+"F0.wireOp",EDGE,"E82.1.5")])],"isStart":true});
            fillet(context, id + "F3", {"entities" : qUnion([Q0]), "radius" : 1 * mm, "tangentPropagation" : true, "allowEdgeOverflow" : false});
        }
    });
